# Revit family: 2025 WUD
name_source: partatom
category: Specialty Equipment
revit_build: Autodesk Revit 2017 (Build: 20160225_1515(x64)
units: mm (PartAtom-declared; Revit-internal decimal feet)

## family parameters
Always vertical = Yes
Cut with Voids When Loaded = No
Part Type = Normal
Room Calculation Point = No
Round Connector Dimension = Use Diameter
Shared = No
Work Plane-Based = No

## types (1)
- 2025 WUD
    Apparent Power = 3600 VA
    Base Height = 25 mm  [stored 0.082021 ft]
    Conn Conduit = Yes
    Cycle = 50 Hz
    Description = DISHWASHER
    FL Amps = 15 A
    Hot Water Size = 1"
    Indirect Waste Size = 2"
    Manufacturer = WASHTECH
    Max Overcurrent Protection = 0 A
    Min Ckt Ampacity = 0 A
    Model = WUD
    Phase = 1
    Volts = 240 V
    Watts = 3600 W
    Weight in kgs = 75

note: [stored X ft] marks values corroborated as IEEE doubles in the binary element streams (Revit-internal decimal feet)

## geometry (parser evidence)
native form markers: Blend x12, Sweep x2
no freeform markers — native parametric forms only
